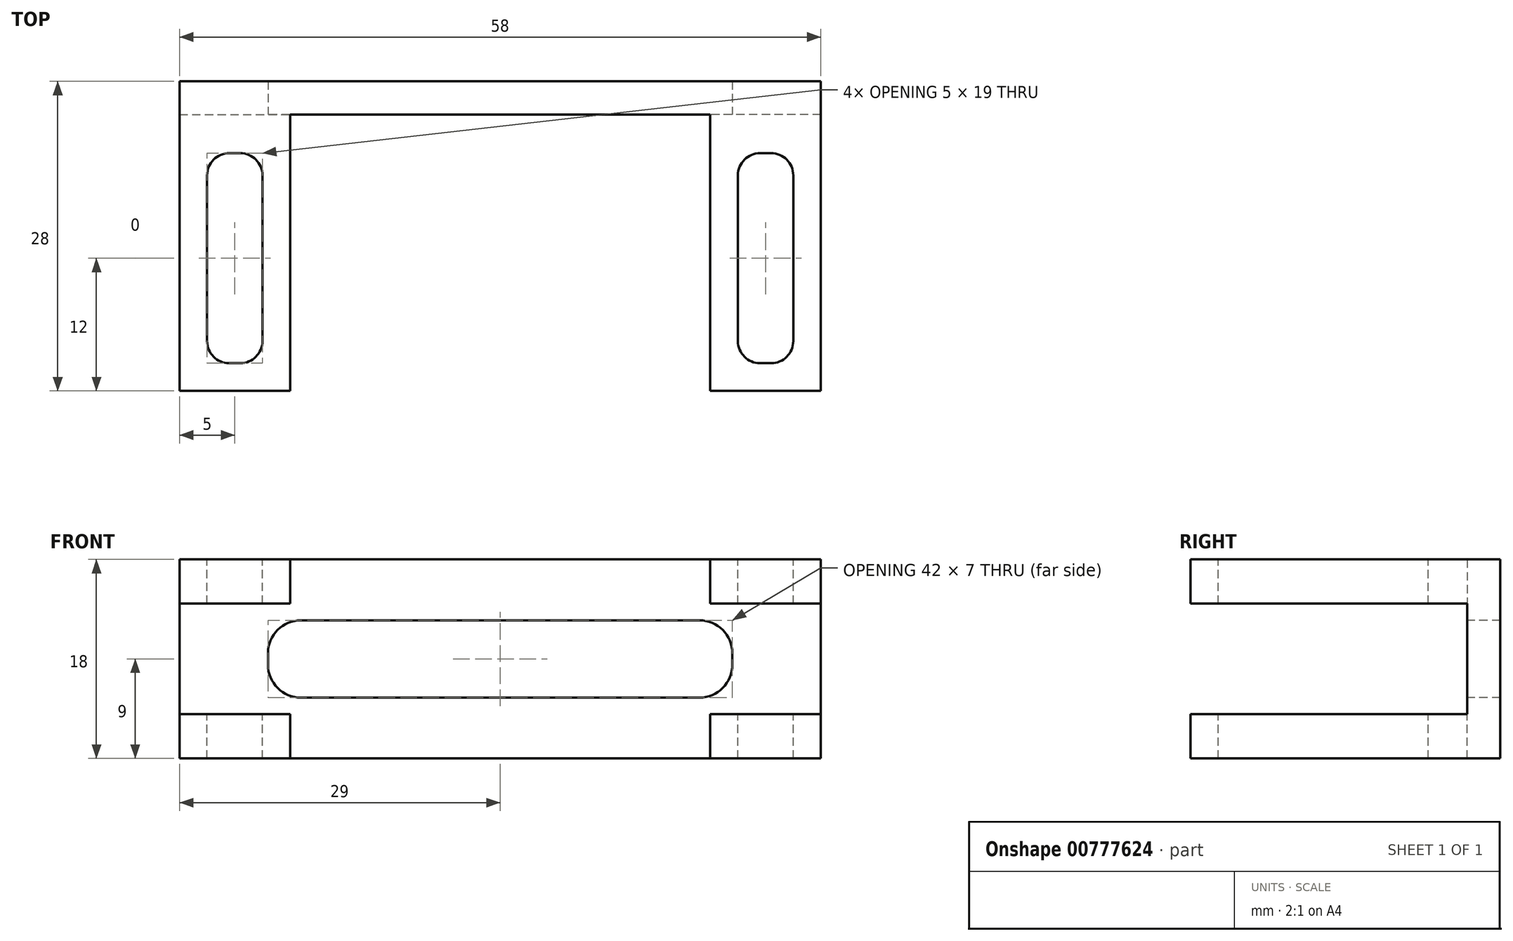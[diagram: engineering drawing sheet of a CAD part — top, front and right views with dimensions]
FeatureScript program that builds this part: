
annotation { "Feature Type Name" : "Feature", "Feature Type Description" : "" }
export const myFeature = defineFeature(function(context is Context, id is Id, definition is map)
    precondition{}
    {
        {
            var Q0;
            Q0=qCreatedBy(makeId("Front.planeOp"),FACE);
            var sketch = newSketch(context, id + "F0", { "sketchPlane" : qUnion([Q0])});
            skLineSegment(sketch, "E0", {"start": v(0, 0) * mm, "end": v(58, 0) * mm});
            skLineSegment(sketch, "E1.0", {"start": v(0, 18) * mm, "end": v(58, 18) * mm});
            skLineSegment(sketch, "E2", {"start": v(0, 18) * mm, "end": v(0, 0) * mm});
            skLineSegment(sketch, "E3", {"start": v(58, 18) * mm, "end": v(58, 0) * mm});
            skSolve(sketch);
        }
        {
            var Q0;
            Q0 = qSketchRegion(id + "F0", true);
            extrude(context, id + "F1", {"entities" : qUnion([Q0]), "depth" : 3 * mm, "offsetDistance" : 25 * mm});
        }
        {
            var Q0;
            Q0=makeQuery(id+"F1.opExtrude","CAP_FACE",FACE,{"disambiguationData":[OSD([sQuery(id+"F0.wireOp",EDGE,"E0"),sQuery(id+"F0.wireOp",EDGE,"E1.0"),sQuery(id+"F0.wireOp",EDGE,"E2"),sQuery(id+"F0.wireOp",EDGE,"E3")])],"isStart":false});
            var sketch = newSketch(context, id + "F2", { "sketchPlane" : qUnion([Q0])});
            skLineSegment(sketch, "E4.bottom", {"start": v(0, 18) * mm, "end": v(10, 18) * mm});
            skLineSegment(sketch, "E4.top", {"start": v(0, 14) * mm, "end": v(10, 14) * mm});
            skLineSegment(sketch, "E4.left", {"start": v(0, 18) * mm, "end": v(0, 14) * mm});
            skLineSegment(sketch, "E4.right", {"start": v(10, 18) * mm, "end": v(10, 14) * mm});
            skLineSegment(sketch, "E5.bottom", {"start": v(0, 0) * mm, "end": v(10, 0) * mm});
            skLineSegment(sketch, "E5.top", {"start": v(0, 4) * mm, "end": v(10, 4) * mm});
            skLineSegment(sketch, "E5.left", {"start": v(0, 0) * mm, "end": v(0, 4) * mm});
            skLineSegment(sketch, "E5.right", {"start": v(10, 0) * mm, "end": v(10, 4) * mm});
            skLineSegment(sketch, "E6.bottom", {"start": v(58, 18) * mm, "end": v(48, 18) * mm});
            skLineSegment(sketch, "E6.top", {"start": v(58, 14) * mm, "end": v(48, 14) * mm});
            skLineSegment(sketch, "E6.left", {"start": v(58, 18) * mm, "end": v(58, 14) * mm});
            skLineSegment(sketch, "E6.right", {"start": v(48, 18) * mm, "end": v(48, 14) * mm});
            skLineSegment(sketch, "E7.bottom", {"start": v(58, 0) * mm, "end": v(48, 0) * mm});
            skLineSegment(sketch, "E7.top", {"start": v(58, 4) * mm, "end": v(48, 4) * mm});
            skLineSegment(sketch, "E7.left", {"start": v(58, 0) * mm, "end": v(58, 4) * mm});
            skLineSegment(sketch, "E7.right", {"start": v(48, 0) * mm, "end": v(48, 4) * mm});
            skSolve(sketch);
        }
        {
            var Q0;
            Q0=makeQuery(id+"F2.imprint","IMPRINT",FACE,{"disambiguationData":[TD([[makeQuery(id+"F2.imprint","IMPRINT",EDGE,{"derivedFrom":sQuery(id+"F2.wireOp",EDGE,"E6.bottom")}),-1.0]])]});
            var Q1;
            Q1=makeQuery(id+"F2.imprint","IMPRINT",FACE,{"disambiguationData":[TD([[makeQuery(id+"F2.imprint","IMPRINT",EDGE,{"derivedFrom":sQuery(id+"F2.wireOp",EDGE,"E7.bottom")}),1.0]])]});
            var Q2;
            Q2=makeQuery(id+"F2.imprint","IMPRINT",FACE,{"disambiguationData":[TD([[makeQuery(id+"F2.imprint","IMPRINT",EDGE,{"derivedFrom":sQuery(id+"F2.wireOp",EDGE,"E5.bottom")}),1.0]])]});
            var Q3;
            Q3=makeQuery(id+"F2.imprint","IMPRINT",FACE,{"disambiguationData":[TD([[makeQuery(id+"F2.imprint","IMPRINT",EDGE,{"derivedFrom":sQuery(id+"F2.wireOp",EDGE,"E4.bottom")}),-1.0]])]});
            extrude(context, id + "F3", {"entities" : qUnion([Q0, Q1, Q2, Q3]), "operationType" : NewBodyOperationType.ADD, "depth" : 25 * mm, "offsetDistance" : 25 * mm});
        }
        {
            var Q0;
            Q0=makeQuery(id+"F1.opExtrude","CAP_FACE",FACE,{"disambiguationData":[OSD([sQuery(id+"F0.wireOp",EDGE,"E0"),sQuery(id+"F0.wireOp",EDGE,"E1.0"),sQuery(id+"F0.wireOp",EDGE,"E2"),sQuery(id+"F0.wireOp",EDGE,"E3")])],"isStart":false});
            var sketch = newSketch(context, id + "F4", { "sketchPlane" : qUnion([Q0])});
            skLineSegment(sketch, "E8.bottom", {"start": v(11, 12.5) * mm, "end": v(47, 12.5) * mm});
            skLineSegment(sketch, "E8.top", {"start": v(11, 5.5) * mm, "end": v(47, 5.5) * mm});
            skLineSegment(sketch, "E8.left", {"start": v(8, 9.5) * mm, "end": v(8, 8.5) * mm});
            skLineSegment(sketch, "E8.right", {"start": v(50, 9.5) * mm, "end": v(50, 8.5) * mm});
            skLineSegment(sketch, "E9", {"start": v(0, 9) * mm, "end": v(58, 9) * mm, "construction": true});
            skLineSegment(sketch, "E10", {"start": v(29, 18) * mm, "end": v(29, 0) * mm, "construction": true});
            skPoint(sketch, "E11.visualSharp", {"position": v(8, 5.5) * mm});
            skArc(sketch, "E11.filletArc", {"start": v(8, 8.5) * mm, "mid": v(8.88, 6.38) * mm, "end": v(11, 5.5) * mm});
            skPoint(sketch, "E12.visualSharp", {"position": v(8, 12.5) * mm});
            skArc(sketch, "E12.filletArc", {"start": v(11, 12.5) * mm, "mid": v(8.88, 11.62) * mm, "end": v(8, 9.5) * mm});
            skPoint(sketch, "E13.visualSharp", {"position": v(50, 12.5) * mm});
            skArc(sketch, "E13.filletArc", {"start": v(50, 9.5) * mm, "mid": v(49.12, 11.62) * mm, "end": v(47, 12.5) * mm});
            skPoint(sketch, "E14.visualSharp", {"position": v(50, 5.5) * mm});
            skArc(sketch, "E14.filletArc", {"start": v(47, 5.5) * mm, "mid": v(49.12, 6.38) * mm, "end": v(50, 8.5) * mm});
            skSolve(sketch);
        }
        {
            var Q0;
            Q0=makeQuery(id+"F4.imprint","IMPRINT",FACE,{"disambiguationData":[TD([[makeQuery(id+"F4.imprint","IMPRINT",EDGE,{"derivedFrom":sQuery(id+"F4.wireOp",EDGE,"E8.bottom")}),-1.0]])]});
            extrude(context, id + "F5", {"entities" : qUnion([Q0]), "operationType" : NewBodyOperationType.REMOVE, "endBound" : BoundingType.THROUGH_ALL, "oppositeDirection" : true, "depth" : 25 * mm, "offsetDistance" : 25 * mm});
        }
        {
            var Q0;
            Q0=makeQuery(id+"F3.boolean.opBoolean","MERGE",FACE,{"derivedFrom":[makeQuery(id+"F1.opExtrude","SWEPT_FACE",FACE,{"disambiguationData":[OSD([sQuery(id+"F0.wireOp",EDGE,"E1.0")])]}),makeQuery(id+"F3.opExtrude","SWEPT_FACE",FACE,{"disambiguationData":[OSD([sQuery(id+"F2.wireOp",EDGE,"E4.bottom")])]}),makeQuery(id+"F3.opExtrude","SWEPT_FACE",FACE,{"disambiguationData":[OSD([sQuery(id+"F2.wireOp",EDGE,"E6.bottom")])]})]});
            var sketch = newSketch(context, id + "F6", { "sketchPlane" : qUnion([Q0])});
            skLineSegment(sketch, "E15.bottom", {"start": v(4.5, -6.5) * mm, "end": v(5.5, -6.5) * mm});
            skLineSegment(sketch, "E15.top", {"start": v(4.5, -25.5) * mm, "end": v(5.5, -25.5) * mm});
            skLineSegment(sketch, "E15.left", {"start": v(2.5, -8.5) * mm, "end": v(2.5, -23.5) * mm});
            skLineSegment(sketch, "E15.right", {"start": v(7.5, -8.5) * mm, "end": v(7.5, -23.5) * mm});
            skLineSegment(sketch, "E16.bottom", {"start": v(52.5, -6.5) * mm, "end": v(53.5, -6.5) * mm});
            skLineSegment(sketch, "E16.top", {"start": v(52.5, -25.5) * mm, "end": v(53.5, -25.5) * mm});
            skLineSegment(sketch, "E16.left", {"start": v(50.5, -8.5) * mm, "end": v(50.5, -23.5) * mm});
            skLineSegment(sketch, "E16.right", {"start": v(55.5, -8.5) * mm, "end": v(55.5, -23.5) * mm});
            skLineSegment(sketch, "E17", {"start": v(29, 0) * mm, "end": v(29, -3) * mm, "construction": true});
            skPoint(sketch, "E18.visualSharp", {"position": v(7.5, -6.5) * mm});
            skArc(sketch, "E18.filletArc", {"start": v(7.5, -8.5) * mm, "mid": v(6.91, -7.09) * mm, "end": v(5.5, -6.5) * mm});
            skPoint(sketch, "E19.visualSharp", {"position": v(2.5, -6.5) * mm});
            skArc(sketch, "E19.filletArc", {"start": v(4.5, -6.5) * mm, "mid": v(3.09, -7.09) * mm, "end": v(2.5, -8.5) * mm});
            skPoint(sketch, "E20.visualSharp", {"position": v(2.5, -25.5) * mm});
            skArc(sketch, "E20.filletArc", {"start": v(2.5, -23.5) * mm, "mid": v(3.09, -24.91) * mm, "end": v(4.5, -25.5) * mm});
            skPoint(sketch, "E21.visualSharp", {"position": v(7.5, -25.5) * mm});
            skArc(sketch, "E21.filletArc", {"start": v(5.5, -25.5) * mm, "mid": v(6.91, -24.91) * mm, "end": v(7.5, -23.5) * mm});
            skPoint(sketch, "E22.visualSharp", {"position": v(50.5, -25.5) * mm});
            skArc(sketch, "E22.filletArc", {"start": v(50.5, -23.5) * mm, "mid": v(51.09, -24.91) * mm, "end": v(52.5, -25.5) * mm});
            skPoint(sketch, "E23.visualSharp", {"position": v(55.5, -25.5) * mm});
            skArc(sketch, "E23.filletArc", {"start": v(53.5, -25.5) * mm, "mid": v(54.91, -24.91) * mm, "end": v(55.5, -23.5) * mm});
            skPoint(sketch, "E24.visualSharp", {"position": v(55.5, -6.5) * mm});
            skArc(sketch, "E24.filletArc", {"start": v(55.5, -8.5) * mm, "mid": v(54.91, -7.09) * mm, "end": v(53.5, -6.5) * mm});
            skPoint(sketch, "E25.visualSharp", {"position": v(50.5, -6.5) * mm});
            skArc(sketch, "E25.filletArc", {"start": v(52.5, -6.5) * mm, "mid": v(51.09, -7.09) * mm, "end": v(50.5, -8.5) * mm});
            skSolve(sketch);
        }
        {
            var Q0;
            Q0=makeQuery(id+"F6.imprint","IMPRINT",FACE,{"disambiguationData":[TD([[makeQuery(id+"F6.imprint","IMPRINT",EDGE,{"derivedFrom":sQuery(id+"F6.wireOp",EDGE,"E15.bottom")}),-1.0]])]});
            var Q1;
            Q1=makeQuery(id+"F6.imprint","IMPRINT",FACE,{"disambiguationData":[TD([[makeQuery(id+"F6.imprint","IMPRINT",EDGE,{"derivedFrom":sQuery(id+"F6.wireOp",EDGE,"E16.bottom")}),-1.0]])]});
            extrude(context, id + "F7", {"entities" : qUnion([Q0, Q1]), "operationType" : NewBodyOperationType.REMOVE, "endBound" : BoundingType.THROUGH_ALL, "oppositeDirection" : true, "depth" : 25 * mm, "offsetDistance" : 25 * mm});
        }
    });
